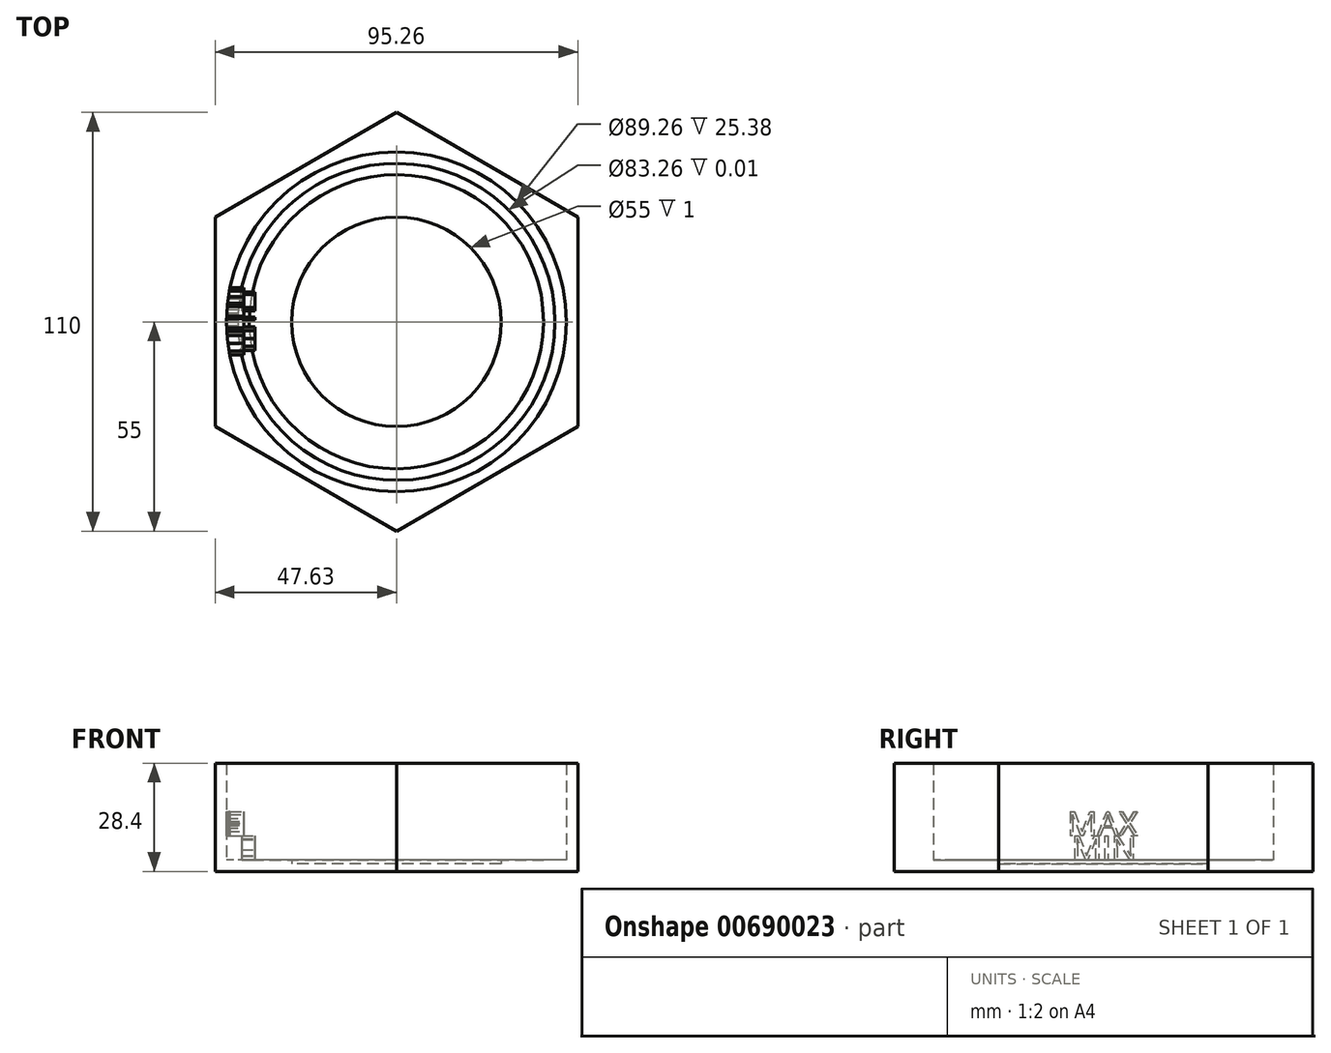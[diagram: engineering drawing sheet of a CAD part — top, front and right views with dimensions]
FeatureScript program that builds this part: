
annotation { "Feature Type Name" : "Feature", "Feature Type Description" : "" }
export const myFeature = defineFeature(function(context is Context, id is Id, definition is map)
    precondition{}
    {
        {
            var Q0;
            Q0=qCreatedBy(makeId("Top.planeOp"),FACE);
            var sketch = newSketch(context, id + "F0", { "sketchPlane" : qUnion([Q0])});
            skCircle(sketch, "E0", {"center": v(0, 0) * mm, "radius": 27.5 * mm});
            skCircle(sketch, "E1.cCircle", {"center": v(0, 0) * mm, "radius": 47.63 * mm, "construction": true});
            skLineSegment(sketch, "E1.0", {"start": v(47.63, -27.5) * mm, "end": v(0, -55) * mm});
            skLineSegment(sketch, "E1.1", {"start": v(0, -55) * mm, "end": v(-47.63, -27.5) * mm});
            skLineSegment(sketch, "E1.2", {"start": v(-47.63, -27.5) * mm, "end": v(-47.63, 27.5) * mm});
            skLineSegment(sketch, "E1.3", {"start": v(-47.63, 27.5) * mm, "end": v(0, 55) * mm});
            skLineSegment(sketch, "E1.4", {"start": v(0, 55) * mm, "end": v(47.63, 27.5) * mm});
            skLineSegment(sketch, "E1.5", {"start": v(47.63, 27.5) * mm, "end": v(47.63, -27.5) * mm});
            skPoint(sketch, "E1.0.midPoint", {"position": v(23.82, -41.25) * mm});
            skSolve(sketch);
        }
        {
            var Q0;
            Q0=makeQuery(id+"F0.imprint","IMPRINT",FACE,{"disambiguationData":[TD([[makeQuery(id+"F0.imprint","IMPRINT",EDGE,{"derivedFrom":sQuery(id+"F0.wireOp",EDGE,"E0")}),-1.0]])]});
            var Q1;
            Q1=makeQuery(id+"F0.imprint","IMPRINT",FACE,{"disambiguationData":[TD([[makeQuery(id+"F0.imprint","IMPRINT",EDGE,{"derivedFrom":sQuery(id+"F0.wireOp",EDGE,"E0")}),1.0]])]});
            extrude(context, id + "F1", {"entities" : qUnion([Q0, Q1]), "depth" : 2 * mm, "offsetDistance" : 25 * mm});
        }
        {
            var Q0;
            Q0=makeQuery(id+"F0.imprint","IMPRINT",FACE,{"disambiguationData":[TD([[makeQuery(id+"F0.imprint","IMPRINT",EDGE,{"derivedFrom":sQuery(id+"F0.wireOp",EDGE,"E0")}),-1.0]])]});
            extrude(context, id + "F2", {"entities" : qUnion([Q0]), "operationType" : NewBodyOperationType.ADD, "depth" : 3 * mm, "offsetDistance" : 25 * mm});
        }
        {
            var Q0;
            Q0=makeQuery(id+"F2.opExtrude","CAP_FACE",FACE,{"disambiguationData":[OSD([sQuery(id+"F0.wireOp",EDGE,"E0"),sQuery(id+"F0.wireOp",EDGE,"E1.0"),sQuery(id+"F0.wireOp",EDGE,"E1.1"),sQuery(id+"F0.wireOp",EDGE,"E1.2"),sQuery(id+"F0.wireOp",EDGE,"E1.3"),sQuery(id+"F0.wireOp",EDGE,"E1.4"),sQuery(id+"F0.wireOp",EDGE,"E1.5")])],"isStart":false});
            var sketch = newSketch(context, id + "F3", { "sketchPlane" : qUnion([Q0])});
            skCircle(sketch, "E2", {"center": v(0, 0) * mm, "radius": 44.63 * mm});
            skSolve(sketch);
        }
        {
            var Q0;
            Q0=makeQuery(id+"F3.imprint","IMPRINT",FACE,{"disambiguationData":[TD([[makeQuery(id+"F3.imprint","IMPRINT",EDGE,{"derivedFrom":sQuery(id+"F3.wireOp",EDGE,"E2")}),-1.0]])]});
            extrude(context, id + "F4", {"entities" : qUnion([Q0]), "operationType" : NewBodyOperationType.ADD, "depth" : 25.4 * mm, "offsetDistance" : 25 * mm});
        }
        {
            var Q0;
            Q0=makeQuery(id+"F2.opExtrude","CAP_FACE",FACE,{"disambiguationData":[OSD([sQuery(id+"F0.wireOp",EDGE,"E0"),sQuery(id+"F0.wireOp",EDGE,"E1.0"),sQuery(id+"F0.wireOp",EDGE,"E1.1"),sQuery(id+"F0.wireOp",EDGE,"E1.2"),sQuery(id+"F0.wireOp",EDGE,"E1.3"),sQuery(id+"F0.wireOp",EDGE,"E1.4"),sQuery(id+"F0.wireOp",EDGE,"E1.5")])],"isStart":false});
            var sketch = newSketch(context, id + "F5", { "sketchPlane" : qUnion([Q0])});
            skCircle(sketch, "E3", {"center": v(0, 0) * mm, "radius": 41.63 * mm});
            skSolve(sketch);
        }
        {
            var Q0;
            Q0=makeQuery(id+"F5.imprint","IMPRINT",FACE,{"disambiguationData":[TD([[makeQuery(id+"F5.imprint","IMPRINT",EDGE,{"derivedFrom":sQuery(id+"F5.wireOp",EDGE,"E3")}),-1.0]])]});
            extrude(context, id + "F6", {"entities" : qUnion([Q0]), "operationType" : NewBodyOperationType.ADD, "depth" : 1 / 50.8 * mm, "offsetDistance" : 25 * mm});
        }
        {
            var Q0;
            Q0=makeQuery(id+"F2.opExtrude","CAP_FACE",FACE,{"disambiguationData":[OSD([sQuery(id+"F0.wireOp",EDGE,"E0"),sQuery(id+"F0.wireOp",EDGE,"E1.0"),sQuery(id+"F0.wireOp",EDGE,"E1.1"),sQuery(id+"F0.wireOp",EDGE,"E1.2"),sQuery(id+"F0.wireOp",EDGE,"E1.3"),sQuery(id+"F0.wireOp",EDGE,"E1.4"),sQuery(id+"F0.wireOp",EDGE,"E1.5")])],"isStart":false});
            var sketch = newSketch(context, id + "F7", { "sketchPlane" : qUnion([Q0])});
            skCircle(sketch, "E4", {"center": v(0, 0) * mm, "radius": 38.63 * mm});
            skSolve(sketch);
        }
        {
            var Q0;
            Q0=makeQuery(id+"F7.imprint","IMPRINT",FACE,{"disambiguationData":[TD([[makeQuery(id+"F7.imprint","IMPRINT",EDGE,{"derivedFrom":sQuery(id+"F7.wireOp",EDGE,"E4")}),-1.0]])]});
            extrude(context, id + "F8", {"entities" : qUnion([Q0]), "operationType" : NewBodyOperationType.ADD, "depth" : 1 / 101.6 * mm, "offsetDistance" : 25 * mm});
        }
        {
            var Q0;
            Q0=qCreatedBy(makeId("Right.planeOp"),FACE);
            var sketch = newSketch(context, id + "F9", { "sketchPlane" : qUnion([Q0])});
            skText(sketch, "E5", { "text": "MIN\n", "fontName": "OpenSans-Regular.ttf"});
            const initialGuessF9  = {"E5": [-0.00839, 0.003, 1, 0, 0.00635]};
            skSetInitialGuess(sketch, initialGuessF9);
            skSolve(sketch);
        }
        {
            var Q0;
            Q0 = qSketchRegion(id + "F9", true);
            extrude(context, id + "F10", {"entities" : qUnion([Q0]), "operationType" : NewBodyOperationType.ADD, "oppositeDirection" : true, "depth" : 40.6 * mm, "offsetDistance" : 25 * mm, "hasSecondDirection" : true, "secondDirectionOppositeDirection" : true, "secondDirectionDepth" : 37.2 * mm});
        }
        {
            var Q0;
            Q0=qCreatedBy(makeId("Right.planeOp"),FACE);
            var sketch = newSketch(context, id + "F11", { "sketchPlane" : qUnion([Q0])});
            skText(sketch, "E6", { "text": "MAX", "fontName": "OpenSans-Regular.ttf"});
            const initialGuessF11  = {"E6": [-0.00959, 0.00935, 1, 0, 0.00635]};
            skSetInitialGuess(sketch, initialGuessF11);
            skSolve(sketch);
        }
        {
            var Q0;
            Q0 = qSketchRegion(id + "F11", true);
            extrude(context, id + "F12", {"entities" : qUnion([Q0]), "operationType" : NewBodyOperationType.ADD, "oppositeDirection" : true, "depth" : 45.5 * mm, "offsetDistance" : 25 * mm, "hasSecondDirection" : true, "secondDirectionOppositeDirection" : true, "secondDirectionDepth" : 40.08 * mm});
        }
    });
